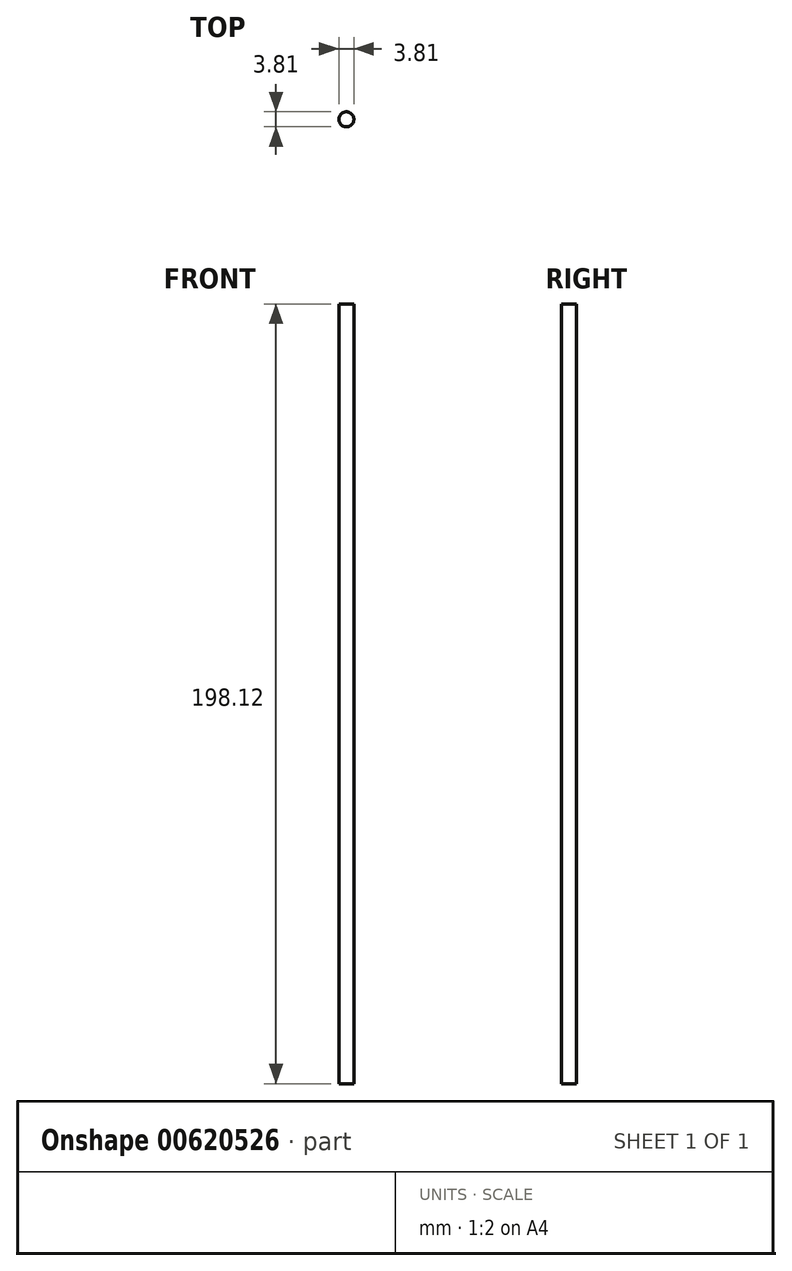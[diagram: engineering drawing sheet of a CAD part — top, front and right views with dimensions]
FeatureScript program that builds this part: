
annotation { "Feature Type Name" : "Feature", "Feature Type Description" : "" }
export const myFeature = defineFeature(function(context is Context, id is Id, definition is map)
    precondition{}
    {
        {
            var Q0;
            Q0=qCreatedBy(makeId("Top.planeOp"),FACE);
            var sketch = newSketch(context, id + "F0", { "sketchPlane" : qUnion([Q0])});
            skCircle(sketch, "E0", {"center": v(-54.61, -11.78) * mm, "radius": 1.9 * mm});
            skSolve(sketch);
        }
        {
            var Q0;
            Q0 = qSketchRegion(id + "F0", true);
            extrude(context, id + "F1", {"entities" : qUnion([Q0]), "depth" : 198.12 * mm, "offsetDistance" : 25.4 * mm});
        }
    });
